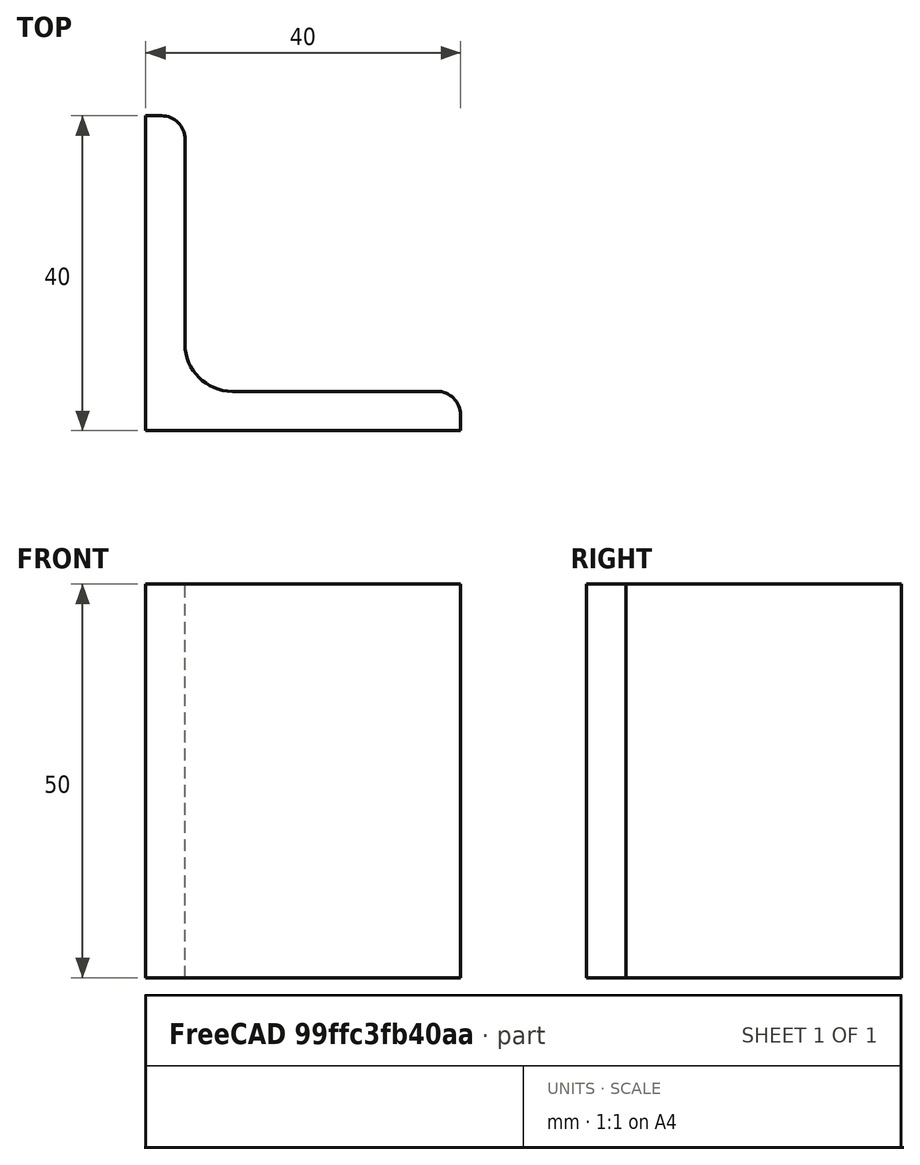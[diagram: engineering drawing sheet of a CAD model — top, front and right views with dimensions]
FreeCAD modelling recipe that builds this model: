
FCSTD DOCUMENT  (FreeCAD 0.15R4671 (Git))
Label: Angle Bar L40x40x5 EN10056 S235JR
License: All rights reserved
LicenseURL: http://en.wikipedia.org/wiki/All_rights_reserved
objects: Sketcher::SketchObject×1, Part::Extrusion×1
note: 2 computed .brp shape members not serialized (recipe doc carries the construction recipe); baked Part::Feature solids carry a one-line shape summary decoded from their .brp

FEATURE [Sketcher::SketchObject] Sketch
  sketch-geometry (9):
    g0: LineSegment StartX=0 StartY=0 StartZ=0 EndX=40 EndY=0 EndZ=0
    g1: LineSegment StartX=40 StartY=0 StartZ=0 EndX=40 EndY=2 EndZ=0
    g2: LineSegment StartX=37 StartY=5 StartZ=0 EndX=11 EndY=5 EndZ=0
    g3: LineSegment StartX=0 StartY=0 StartZ=0 EndX=0 EndY=40 EndZ=0
    g4: LineSegment StartX=0 StartY=40 StartZ=0 EndX=2 EndY=40 EndZ=0
    g5: LineSegment StartX=5 StartY=37 StartZ=0 EndX=5 EndY=11 EndZ=0
    g6: ArcOfCircle CenterX=11 CenterY=11 CenterZ=0 NormalX=0 NormalY=0 NormalZ=1 Radius=6 StartAngle=3.14159 EndAngle=4.71239
    g7: ArcOfCircle CenterX=2 CenterY=37 CenterZ=0 NormalX=0 NormalY=0 NormalZ=1 Radius=3 StartAngle=0 EndAngle=1.5708
    g8: ArcOfCircle CenterX=37 CenterY=2 CenterZ=0 NormalX=0 NormalY=0 NormalZ=1 Radius=3 StartAngle=0 EndAngle=1.5708
  constraints (23):
    c: Coincident(g0,g-1)
    c: Horizontal(g0)
    c: Coincident(g1,g0)
    c: Vertical(g1)
    c: Horizontal(g2)
    c: Coincident(g3,g-1)
    c: Vertical(g3)
    c: Coincident(g4,g3)
    c: Horizontal(g4)
    c: Vertical(g5)
    c: Tangent(g5,g6) = -1.5708
    c: Tangent(g2,g6) = 1.5708
    c: Tangent(g4,g7) = 1.5708
    c: Tangent(g5,g7) = 1.5708
    c: Tangent(g2,g8) = -1.5708
    c: Tangent(g1,g8) = -1.5708
    c: DistanceX(g0) = 40
    c: DistanceY(g3) = 40
    c: DistanceY(g0,g2) = 5
    c: DistanceX(g3,g5) = 5
    c: Radius(g6) = 6
    c: Radius(g8) = 3
    c: Radius(g7) = 3
FEATURE [Part::Extrusion] Extrude  label="Angle Bar L40x40x5 EN10056 S235JR"
  Base = -> Sketch
  Dir = (0,0,50)
  Solid = true
